# Revit family: M321
name_source: partatom
category: Generic Models
revit_build: Autodesk Revit 2018 (Build: 20170223_1515(x64)
units: mm (PartAtom-declared; Revit-internal decimal feet)

## family parameters
Always vertical = Yes
Can host rebar = No
Cut with Voids When Loaded = No
Part Type = Normal
Room Calculation Point = No
Round Connector Dimension = Use Diameter
Shared = No
Work Plane-Based = No

## types (2) — shared parameters
CONNECTIVITY- Input Terminals- Data = USB 2.0 (Media Player, 5V/2A)
CONNECTIVITY- Input Terminals- Digital = HDMI 2.0 x2, DP 1.2 x1
CONNECTIVITY- Input Terminals- External Control = LAN (100Mbit), 3.5mm Mini Jack IR Remote, RS-232C
CONNECTIVITY- Output Terminals- Audio = 3.5mm Mini Jack
Description = 32 in. Professional Grade Large Format Display
ENVIRONMENTAL CONDITIONS- Operating Altitude = 3000m (9843ft)
ENVIRONMENTAL CONDITIONS- Operating Humidity = 20-80%
ENVIRONMENTAL CONDITIONS- Operating Temperature = 0 to 40C
LCD MODULE- Aspect Ratio = 16:9
LCD MODULE- Brightness (Typiical) = 450 cd/m2
LCD MODULE- Color Gamut = 68% NTSC (TBD)
LCD MODULE- Contrast Ratio (Typical) = 1100:1
LCD MODULE- Displayable Colors = Over 16.7 Million (8bit)
LCD MODULE- Native Resolution = 1920 x 1080
LCD MODULE- Orientation = Landscape and Portrait (CCW Rotation)
LCD MODULE- Panel Haze (%) = 28
LCD MODULE- Panel Technology = IPS
LCD MODULE- Viewable Image Size = 32 in.
LCD MODULE- Viewing Angle = 178° Vert., 178° Hor. (89U/89D/89L/89R) @ CR>10
Manufacturer = NEC Display Solutions
Model = NEC MultiSync® M321
PHYSICAL SPECS- Bezel Width (L/R, T/B) = 11.9mm/11.9mm/11.8mm/17.2mm
PHYSICAL SPECS- Net Dimensions (w/o Stand, WxHxD) = 28.6 x 16.8 x 2.6 in (726.5 x 425.4 x 66.5mm)
PHYSICAL SPECS- Net Weight (w/o Stand) = 6.3kg / 13.9lbs.
PHYSICAL SPECS- Vesa Hole Configuration = 100mm x 100mm (4 x M4 x 14mm), 200 x 200 (4 x M4 x 10mm, off-center)
POWER CONSUMPTION- Current Rating = 0.8A - 0.3A @ 100V - 240V
POWER CONSUMPTION- Network Standby = 2W
POWER CONSUMPTION- Normal Standby = <0.5W
POWER CONSUMPTION- On (Typ/Max Bightness/Overall Max) = 40W/50W/75W
POWER CONSUMPTION- Speaker Rating = Integrated 5W x 5W
SENSORS- Ambient Light Sensor = Optional (KT-RC3)
SENSORS- Human Sensor = Optional (KT-RC3)
SENSORS- Temperature Sensor = Integrated and programmable
Type Image = M321.png
URL = https://www.sharpnecdisplays.us

## per-type parameters (varying)
| type | Stand No | Stand Yes |
| with Stand | No | Yes |
| no Stand | Yes | No |

## geometry (parser evidence)
native form markers: Sweep x2
no freeform markers — native parametric forms only
